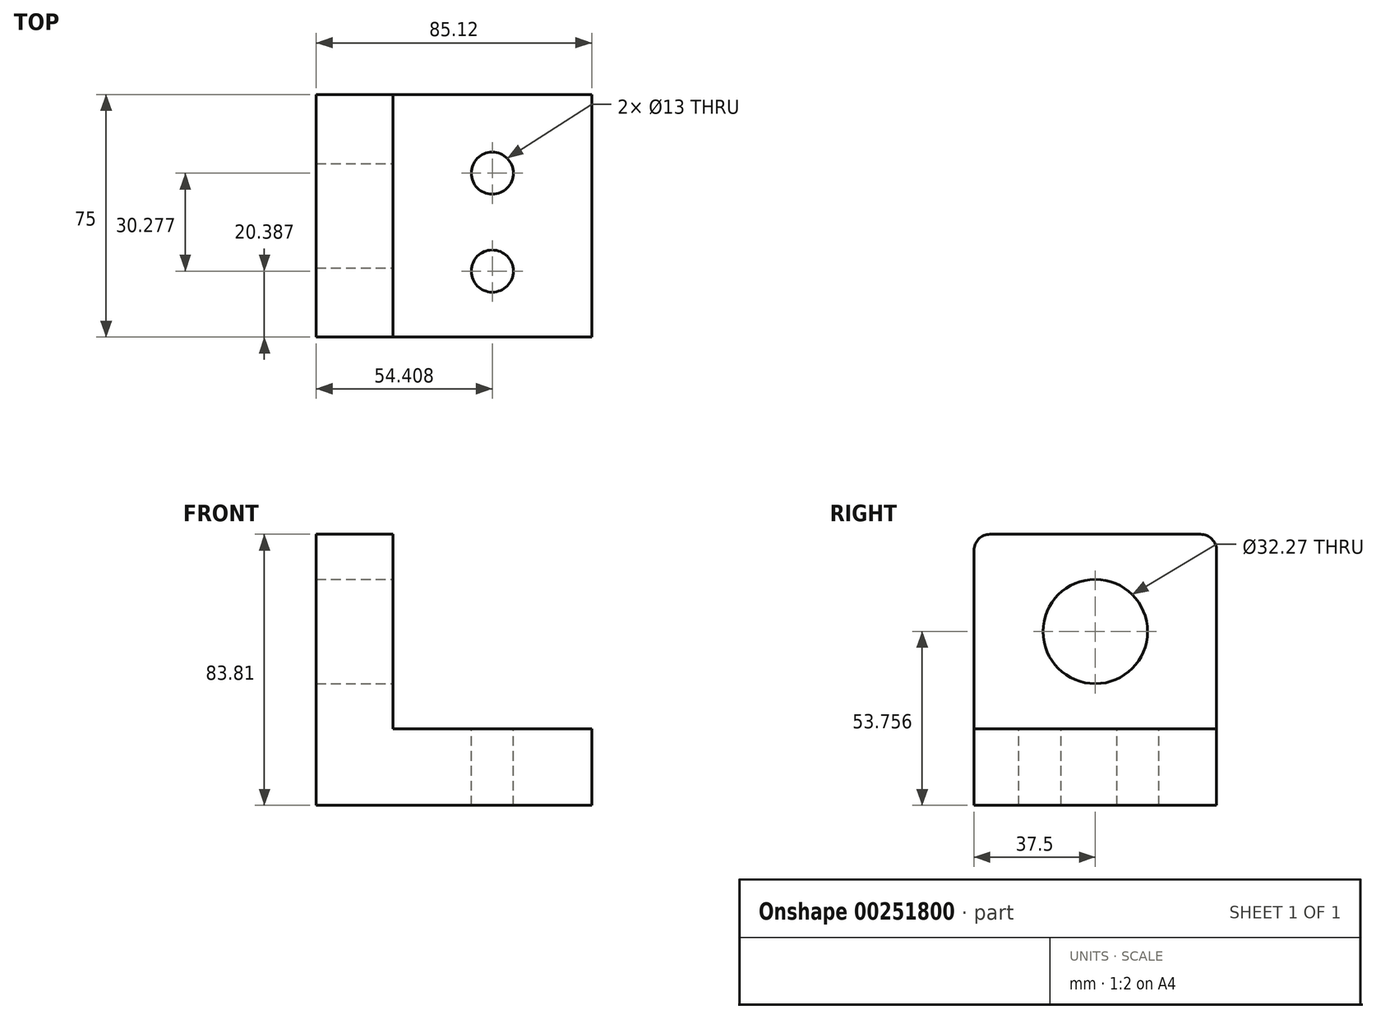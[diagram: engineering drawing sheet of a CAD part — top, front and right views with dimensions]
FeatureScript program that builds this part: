
annotation { "Feature Type Name" : "Feature", "Feature Type Description" : "" }
export const myFeature = defineFeature(function(context is Context, id is Id, definition is map)
    precondition{}
    {
        {
            var Q0;
            Q0=qCreatedBy(makeId("Front.planeOp"),FACE);
            var sketch = newSketch(context, id + "F0", { "sketchPlane" : qUnion([Q0])});
            skLineSegment(sketch, "E0.bottom", {"start": v(42.56, -11.85) * mm, "end": v(-42.56, -11.85) * mm});
            skLineSegment(sketch, "E0.top", {"start": v(42.56, 11.85) * mm, "end": v(-42.56, 11.85) * mm});
            skLineSegment(sketch, "E0.left", {"start": v(42.56, -11.85) * mm, "end": v(42.56, 11.85) * mm});
            skLineSegment(sketch, "E0.right", {"start": v(-42.56, -11.85) * mm, "end": v(-42.56, 11.85) * mm});
            skPoint(sketch, "E0.middle", {"position": v(0, 0) * mm});
            skLineSegment(sketch, "E1.bottom", {"start": v(-42.56, 11.85) * mm, "end": v(-18.87, 11.85) * mm});
            skLineSegment(sketch, "E1.top", {"start": v(-42.56, 71.96) * mm, "end": v(-18.87, 71.96) * mm});
            skLineSegment(sketch, "E1.left", {"start": v(-42.56, 11.85) * mm, "end": v(-42.56, 71.96) * mm});
            skLineSegment(sketch, "E1.right", {"start": v(-18.87, 11.85) * mm, "end": v(-18.87, 71.96) * mm});
            skSolve(sketch);
        }
        {
            var Q0;
            Q0 = qSketchRegion(id + "F0", true);
            extrude(context, id + "F1", {"entities" : qUnion([Q0]), "oppositeDirection" : true, "depth" : 75 * mm});
        }
        {
            var Q0;
            Q0=makeQuery(id+"F1.opExtrude","SWEPT_FACE",FACE,{"disambiguationData":[OSD([sQuery(id+"F0.wireOp",EDGE,"E1.right")])]});
            var sketch = newSketch(context, id + "F2", { "sketchPlane" : qUnion([Q0])});
            skCircle(sketch, "E2", {"center": v(37.5, 41.9) * mm, "radius": 16.13 * mm});
            skPoint(sketch, "E2.centerSnap0", {"position": v(37.5, 71.96) * mm});
            skPoint(sketch, "E2.centerSnap1", {"position": v(0, 41.9) * mm});
            skSolve(sketch);
        }
        {
            var Q0;
            Q0 = qSketchRegion(id + "F2", true);
            extrude(context, id + "F3", {"entities" : qUnion([Q0]), "operationType" : NewBodyOperationType.REMOVE, "endBound" : BoundingType.THROUGH_ALL, "oppositeDirection" : true, "depth" : 25 * mm});
        }
        {
            var Q0;
            Q0=makeQuery(id+"F1.opExtrude","SWEPT_FACE",FACE,{"disambiguationData":[OSD([sQuery(id+"F0.wireOp",EDGE,"E0.top")])]});
            var sketch = newSketch(context, id + "F4", { "sketchPlane" : qUnion([Q0])});
            skCircle(sketch, "E3", {"center": v(11.85, 20.39) * mm, "radius": 6.5 * mm});
            skPoint(sketch, "E3.centerSnap0", {"position": v(11.85, 0) * mm});
            skCircle(sketch, "E4", {"center": v(11.85, 50.66) * mm, "radius": 6.5 * mm});
            skPoint(sketch, "E4.centerSnap0", {"position": v(11.85, 75) * mm});
            skSolve(sketch);
        }
        {
            var Q0;
            Q0 = qSketchRegion(id + "F4", true);
            extrude(context, id + "F5", {"entities" : qUnion([Q0]), "operationType" : NewBodyOperationType.REMOVE, "endBound" : BoundingType.THROUGH_ALL, "oppositeDirection" : true, "depth" : 25 * mm});
        }
        {
            var Q0;
            Q0=makeQuery(id+"F1.opExtrude","CAP_EDGE",EDGE,{"disambiguationData":[OSD([sQuery(id+"F0.wireOp",EDGE,"E1.top")])],"isStart":true});
            var Q1;
            Q1=makeQuery(id+"F1.opExtrude","CAP_EDGE",EDGE,{"disambiguationData":[OSD([sQuery(id+"F0.wireOp",EDGE,"E1.top")])],"isStart":false});
            fillet(context, id + "F6", {"entities" : qUnion([Q0, Q1]), "radius" : 5 * mm, "tangentPropagation" : true, "allowEdgeOverflow" : false});
        }
    });
